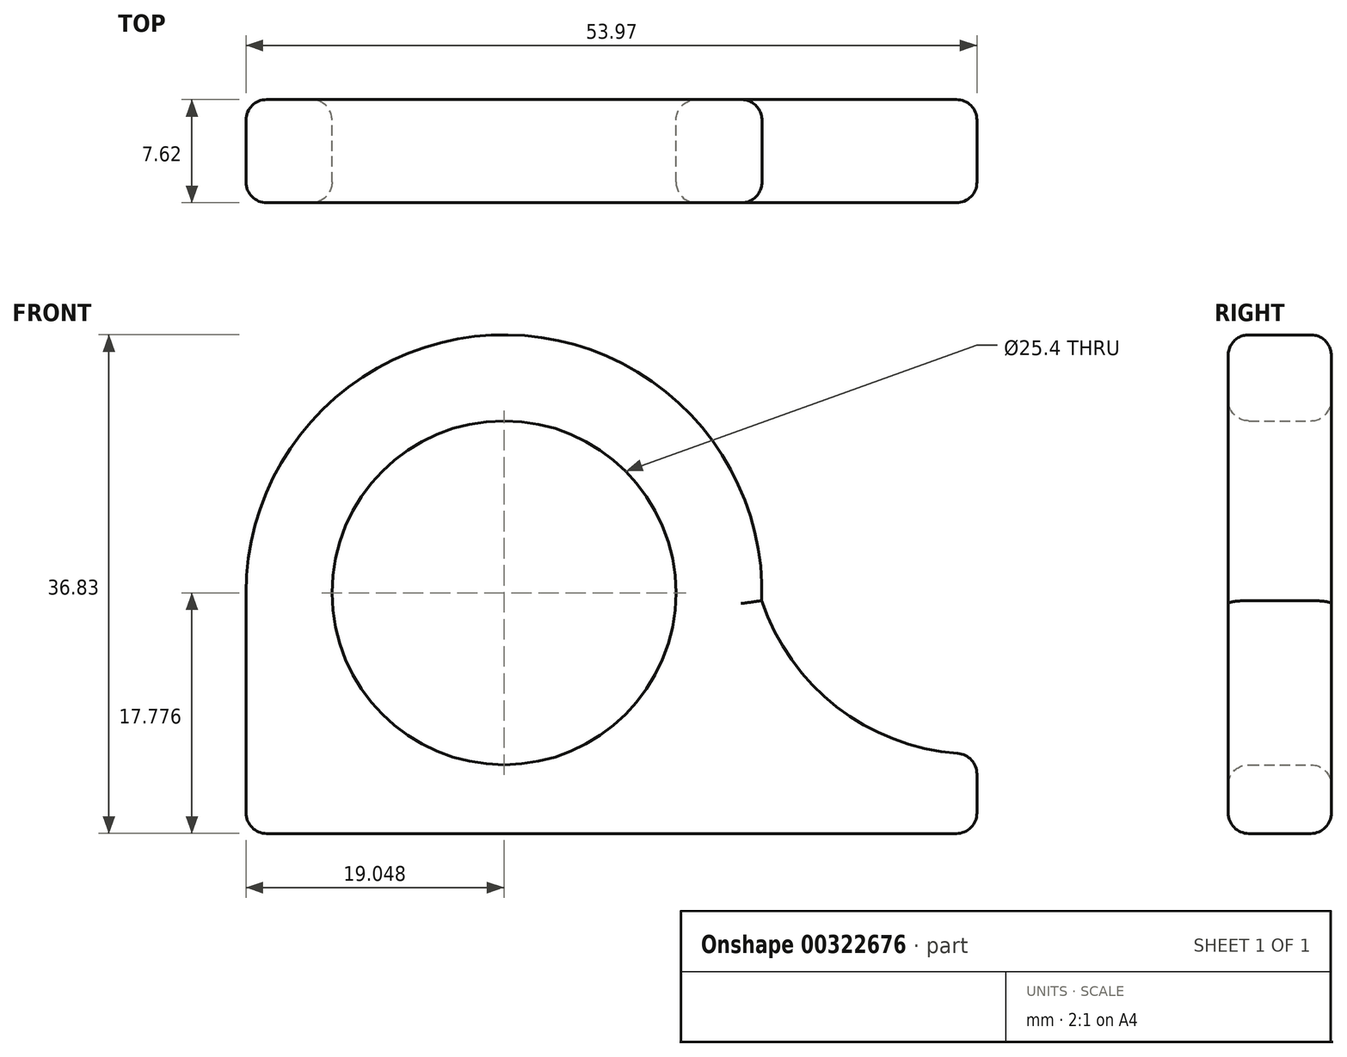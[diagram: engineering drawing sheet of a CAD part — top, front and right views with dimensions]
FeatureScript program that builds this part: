
annotation { "Feature Type Name" : "Feature", "Feature Type Description" : "" }
export const myFeature = defineFeature(function(context is Context, id is Id, definition is map)
    precondition{}
    {
        {
            var Q0;
            Q0=qCreatedBy(makeId("Front.planeOp"),FACE);
            var sketch = newSketch(context, id + "F0", { "sketchPlane" : qUnion([Q0])});
            skCircle(sketch, "E0", {"center": v(-47.23, 39.53) * mm, "radius": 12.7 * mm});
            skLineSegment(sketch, "E1", {"start": v(-66.28, 21.75) * mm, "end": v(-12.3, 21.75) * mm});
            skLineSegment(sketch, "E2", {"start": v(-12.3, 21.75) * mm, "end": v(-12.3, 27.61) * mm});
            skArc(sketch, "E3", {"start": v(-28.2, 38.94) * mm, "mid": v(-22.1, 30.68) * mm, "end": v(-12.3, 27.61) * mm});
            skLineSegment(sketch, "E4", {"start": v(-66.28, 21.75) * mm, "end": v(-66.28, 39.53) * mm});
            skArc(sketch, "E5", {"start": v(-28.2, 38.94) * mm, "mid": v(-46.94, 58.57) * mm, "end": v(-66.28, 39.53) * mm});
            skSolve(sketch);
        }
        {
            var Q0;
            Q0=makeQuery(id+"F0.imprint","IMPRINT",FACE,{"disambiguationData":[TD([[makeQuery(id+"F0.imprint","IMPRINT",EDGE,{"derivedFrom":sQuery(id+"F0.wireOp",EDGE,"E0")}),-1.0]])]});
            extrude(context, id + "F1", {"entities" : qUnion([Q0]), "depth" : 7.62 * mm});
        }
        {
            var Q0;
            Q0=makeQuery(id+"F1.opExtrude","CAP_EDGE",EDGE,{"disambiguationData":[OSD([sQuery(id+"F0.wireOp",EDGE,"E0")])],"isStart":false});
            var Q1;
            Q1=makeQuery(id+"F1.opExtrude","CAP_EDGE",EDGE,{"disambiguationData":[OSD([sQuery(id+"F0.wireOp",EDGE,"2f2dc564-4f0b-41e5-87b1-d57f499f364b")])],"isStart":false});
            var Q2;
            Q2=makeQuery(id+"F1.opExtrude","CAP_EDGE",EDGE,{"disambiguationData":[OSD([sQuery(id+"F0.wireOp",EDGE,"E1")])],"isStart":false});
            var Q3;
            Q3=makeQuery(id+"F1.opExtrude","CAP_EDGE",EDGE,{"disambiguationData":[OSD([sQuery(id+"F0.wireOp",EDGE,"E2")])],"isStart":false});
            var Q4;
            Q4=makeQuery(id+"F1.opExtrude","SWEPT_EDGE",EDGE,{"disambiguationData":[OSD([sQuery(id+"F0.wireOp",EDGE,"E2"),sQuery(id+"F0.wireOp",EDGE,"2f2dc564-4f0b-41e5-87b1-d57f499f364b")])]});
            var Q5;
            Q5=makeQuery(id+"F1.opExtrude","SWEPT_EDGE",EDGE,{"disambiguationData":[OSD([sQuery(id+"F0.wireOp",EDGE,"E1"),sQuery(id+"F0.wireOp",EDGE,"E2")])]});
            var Q6;
            Q6=makeQuery(id+"F1.opExtrude","CAP_EDGE",EDGE,{"disambiguationData":[OSD([sQuery(id+"F0.wireOp",EDGE,"E1")])],"isStart":true});
            var Q7;
            Q7=makeQuery(id+"F1.opExtrude","CAP_EDGE",EDGE,{"disambiguationData":[OSD([sQuery(id+"F0.wireOp",EDGE,"E2")])],"isStart":true});
            var Q8;
            Q8=makeQuery(id+"F1.opExtrude","CAP_EDGE",EDGE,{"disambiguationData":[OSD([sQuery(id+"F0.wireOp",EDGE,"2f2dc564-4f0b-41e5-87b1-d57f499f364b")])],"isStart":true});
            var Q9;
            Q9=makeQuery(id+"F1.opExtrude","CAP_EDGE",EDGE,{"disambiguationData":[OSD([sQuery(id+"F0.wireOp",EDGE,"E0")])],"isStart":true});
            var Q10;
            Q10=makeQuery(id+"F1.opExtrude","SWEPT_EDGE",EDGE,{"disambiguationData":[OSD([sQuery(id+"F0.wireOp",EDGE,"E1"),sQuery(id+"F0.wireOp",EDGE,"2f2dc564-4f0b-41e5-87b1-d57f499f364b")])]});
            var Q11;
            Q11=makeQuery(id+"F1.opExtrude","CAP_EDGE",EDGE,{"disambiguationData":[OSD([sQuery(id+"F0.wireOp",EDGE,"E5")])],"isStart":false});
            var Q12;
            Q12=makeQuery(id+"F1.opExtrude","CAP_EDGE",EDGE,{"disambiguationData":[OSD([sQuery(id+"F0.wireOp",EDGE,"E3")])],"isStart":false});
            var Q13;
            Q13=makeQuery(id+"F1.opExtrude","CAP_EDGE",EDGE,{"disambiguationData":[OSD([sQuery(id+"F0.wireOp",EDGE,"E3")])],"isStart":true});
            var Q14;
            Q14=makeQuery(id+"F1.opExtrude","CAP_EDGE",EDGE,{"disambiguationData":[OSD([sQuery(id+"F0.wireOp",EDGE,"E5")])],"isStart":true});
            fillet(context, id + "F2", {"entities" : qUnion([Q0, Q1, Q2, Q3, Q4, Q5, Q6, Q7, Q8, Q9, Q10, Q11, Q12, Q13, Q14]), "radius" : 1.52 * mm, "tangentPropagation" : true, "allowEdgeOverflow" : false});
        }
    });
